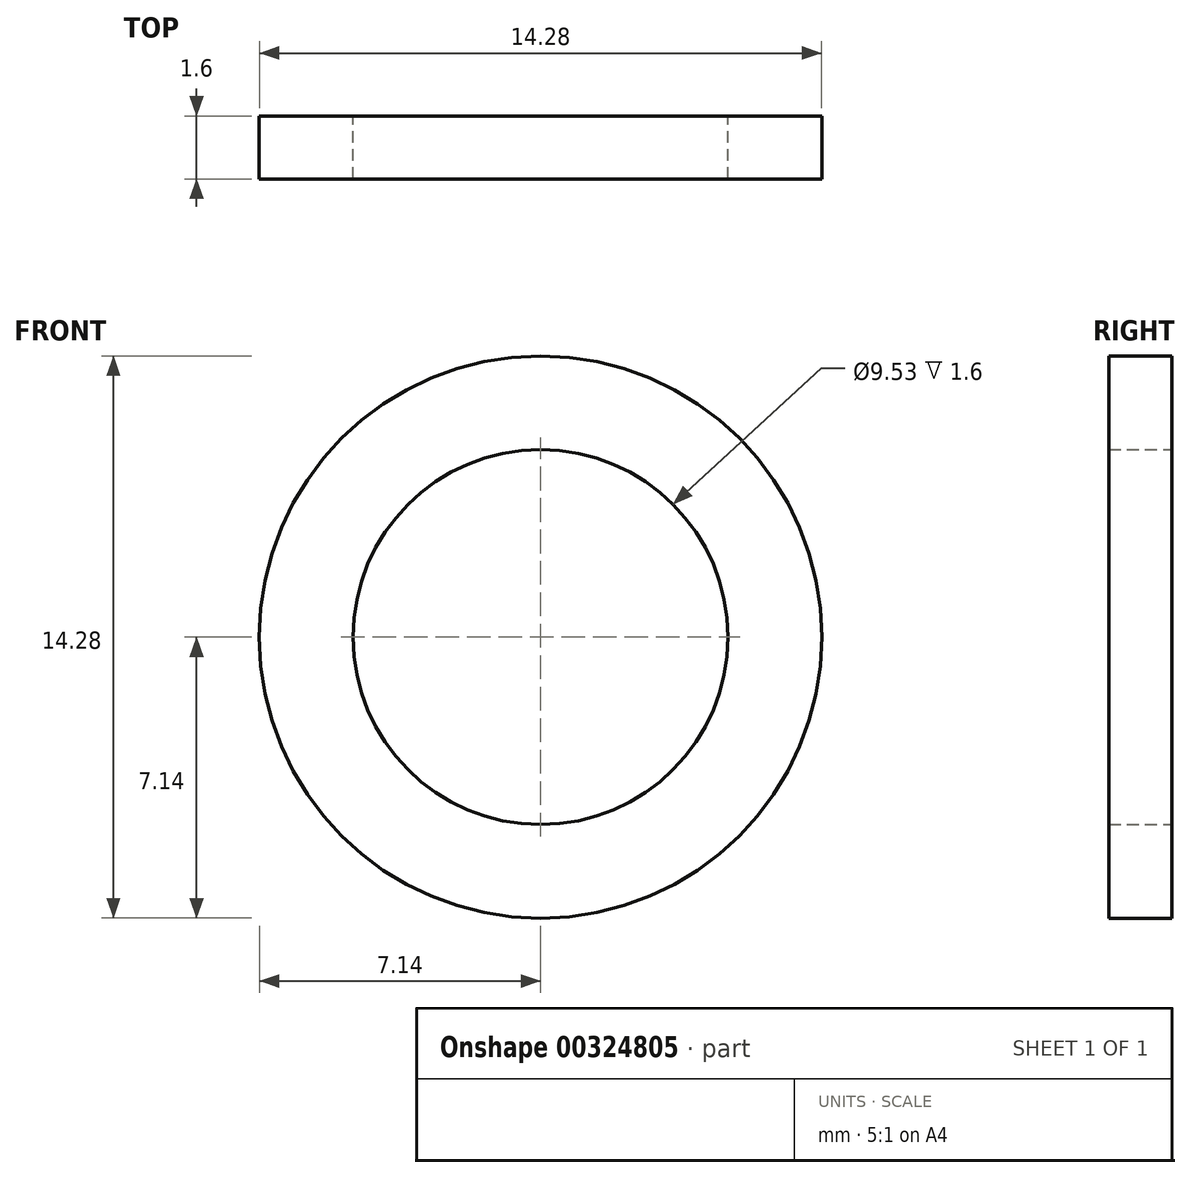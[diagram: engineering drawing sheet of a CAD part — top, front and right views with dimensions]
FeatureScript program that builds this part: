
annotation { "Feature Type Name" : "Feature", "Feature Type Description" : "" }
export const myFeature = defineFeature(function(context is Context, id is Id, definition is map)
    precondition{}
    {
        {
            var Q0;
            Q0=qCreatedBy(makeId("Front.planeOp"),FACE);
            var sketch = newSketch(context, id + "F0", { "sketchPlane" : qUnion([Q0])});
            skCircle(sketch, "E0", {"center": v(0, 0) * mm, "radius": 7.14 * mm});
            skCircle(sketch, "E1", {"center": v(0, 0) * mm, "radius": 4.76 * mm});
            skSolve(sketch);
        }
        {
            var Q0;
            Q0=makeQuery(id+"F0.imprint","IMPRINT",FACE,{"disambiguationData":[TD([[makeQuery(id+"F0.imprint","IMPRINT",EDGE,{"derivedFrom":sQuery(id+"F0.wireOp",EDGE,"E0")}),1.0]])]});
            extrude(context, id + "F1", {"entities" : qUnion([Q0]), "depth" : 1.6 * mm, "offsetDistance" : 25.4 * mm});
        }
    });
